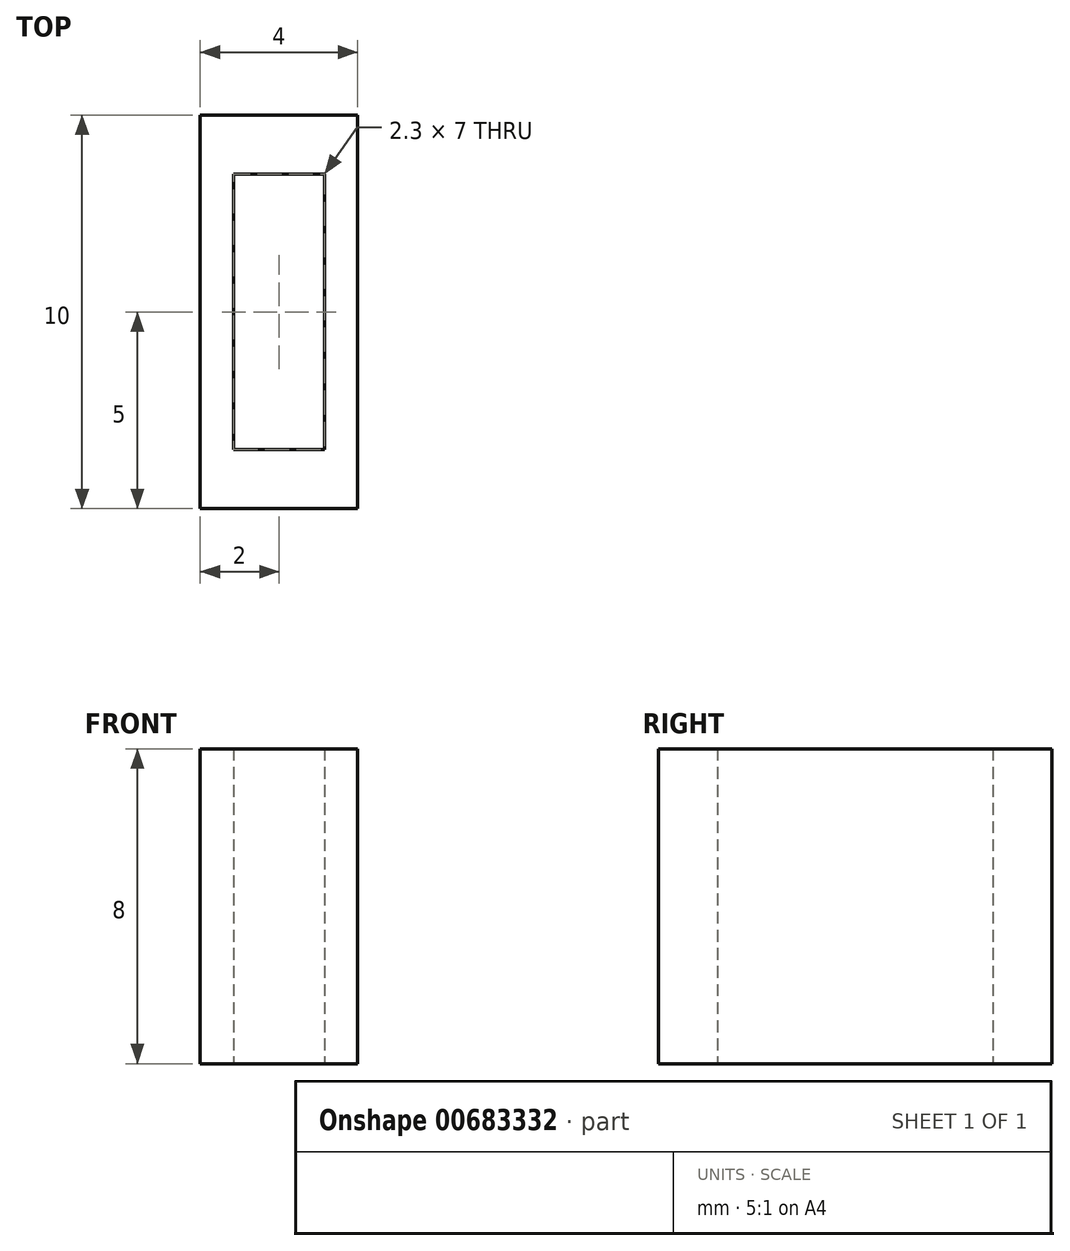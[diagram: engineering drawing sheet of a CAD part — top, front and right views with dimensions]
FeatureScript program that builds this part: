
annotation { "Feature Type Name" : "Feature", "Feature Type Description" : "" }
export const myFeature = defineFeature(function(context is Context, id is Id, definition is map)
    precondition{}
    {
        {
            var Q0;
            Q0=qCreatedBy(makeId("Top.planeOp"),FACE);
            var sketch = newSketch(context, id + "F0", { "sketchPlane" : qUnion([Q0])});
            skLineSegment(sketch, "E0.bottom", {"start": v(1.15, 3.5) * mm, "end": v(-1.15, 3.5) * mm});
            skLineSegment(sketch, "E0.top", {"start": v(1.15, -3.5) * mm, "end": v(-1.15, -3.5) * mm});
            skLineSegment(sketch, "E0.left", {"start": v(1.15, 3.5) * mm, "end": v(1.15, -3.5) * mm});
            skLineSegment(sketch, "E0.right", {"start": v(-1.15, 3.5) * mm, "end": v(-1.15, -3.5) * mm});
            skPoint(sketch, "E0.middle", {"position": v(0, 0) * mm});
            skLineSegment(sketch, "E1.bottom", {"start": v(2, 5) * mm, "end": v(-2, 5) * mm});
            skLineSegment(sketch, "E1.top", {"start": v(2, -5) * mm, "end": v(-2, -5) * mm});
            skLineSegment(sketch, "E1.left", {"start": v(2, 5) * mm, "end": v(2, -5) * mm});
            skLineSegment(sketch, "E1.right", {"start": v(-2, 5) * mm, "end": v(-2, -5) * mm});
            skSolve(sketch);
        }
        {
            var Q0;
            Q0 = qSketchRegion(id + "F0", true);
            extrude(context, id + "F1", {"entities" : qUnion([Q0]), "depth" : 8 * mm, "offsetDistance" : 25 * mm});
        }
    });
